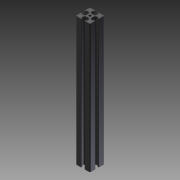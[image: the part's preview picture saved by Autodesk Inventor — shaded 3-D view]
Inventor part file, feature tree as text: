
AUTODESK INVENTOR PART (.ipt)
format: ipt  version: 2011 SP1 (Build 150282100, 282)  size: 143,360 bytes
history: native  units: mm
features: extrude x1, sketch x1
ambient origin geometry x8: Origin, YZ Plane, XZ Plane, XY Plane, X Axis, Y Axis, Z Axis, Center Point
bodies: Solid1 (feature_tree)
feature tree (2):
  extrude  "Extrusion1"  [1 undecoded]
  sketch  "Sketch_1"  dims[d0=136.0mm d1=0.0mm]
note: 1 required parameter value undecoded (feature->parameter linkage not recoverable at this tier; creation-order binding heuristic only, values carry confidence <= 0.55)
